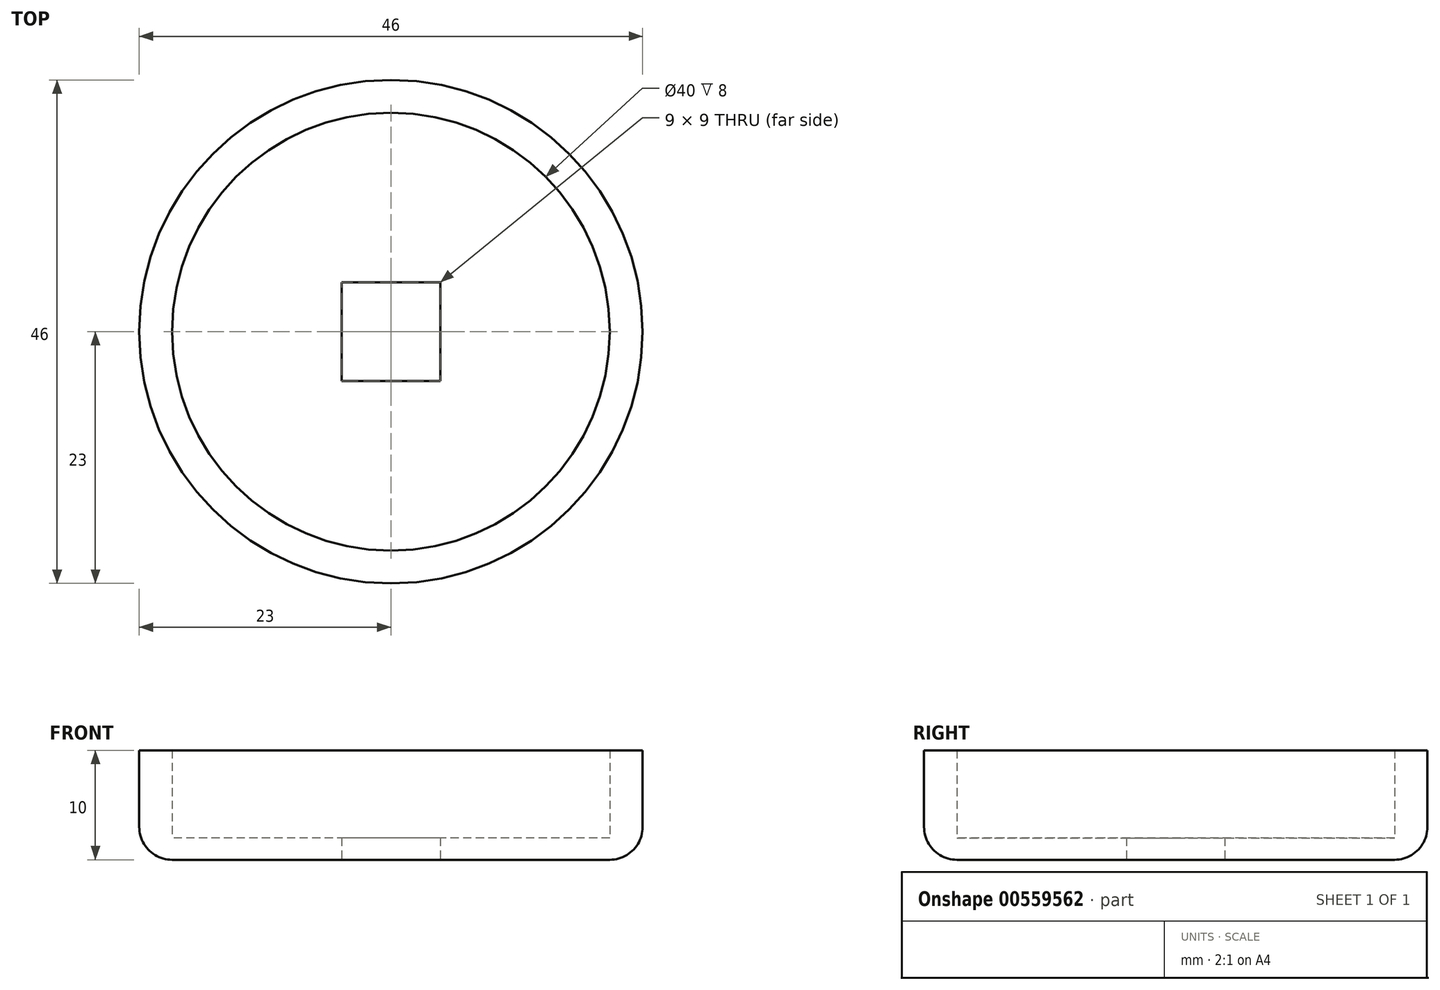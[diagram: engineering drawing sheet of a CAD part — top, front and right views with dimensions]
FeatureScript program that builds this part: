
annotation { "Feature Type Name" : "Feature", "Feature Type Description" : "" }
export const myFeature = defineFeature(function(context is Context, id is Id, definition is map)
    precondition{}
    {
        {
            var Q0;
            Q0=qCreatedBy(makeId("Top.planeOp"),FACE);
            var sketch = newSketch(context, id + "F0", { "sketchPlane" : qUnion([Q0])});
            skCircle(sketch, "E0", {"center": v(0, 0) * mm, "radius": 20 * mm});
            skCircle(sketch, "E1.0", {"center": v(0, 0) * mm, "radius": 23 * mm});
            skLineSegment(sketch, "E2.bottom", {"start": v(4.5, -4.5) * mm, "end": v(-4.5, -4.5) * mm});
            skLineSegment(sketch, "E2.top", {"start": v(4.5, 4.5) * mm, "end": v(-4.5, 4.5) * mm});
            skLineSegment(sketch, "E2.left", {"start": v(4.5, -4.5) * mm, "end": v(4.5, 4.5) * mm});
            skLineSegment(sketch, "E2.right", {"start": v(-4.5, -4.5) * mm, "end": v(-4.5, 4.5) * mm});
            skSolve(sketch);
        }
        {
            var Q0;
            Q0=makeQuery(id+"F0.imprint","IMPRINT",FACE,{"disambiguationData":[TD([[makeQuery(id+"F0.imprint","IMPRINT",EDGE,{"derivedFrom":sQuery(id+"F0.wireOp",EDGE,"E0")}),-1.0]])]});
            extrude(context, id + "F1", {"entities" : qUnion([Q0]), "depth" : 10 * mm, "offsetDistance" : 25 * mm});
        }
        {
            var Q0;
            Q0=qCreatedBy(makeId("Top.planeOp"),FACE);
            var sketch = newSketch(context, id + "F2", { "sketchPlane" : qUnion([Q0])});
            skCircle(sketch, "E3", {"center": v(0, 0) * mm, "radius": 20 * mm});
            skLineSegment(sketch, "E4.bottom", {"start": v(4.5, -4.5) * mm, "end": v(-4.5, -4.5) * mm});
            skLineSegment(sketch, "E4.top", {"start": v(4.5, 4.5) * mm, "end": v(-4.5, 4.5) * mm});
            skLineSegment(sketch, "E4.left", {"start": v(4.5, -4.5) * mm, "end": v(4.5, 4.5) * mm});
            skLineSegment(sketch, "E4.right", {"start": v(-4.5, -4.5) * mm, "end": v(-4.5, 4.5) * mm});
            skSolve(sketch);
        }
        {
            var Q0;
            Q0=makeQuery(id+"F2.imprint","IMPRINT",FACE,{"disambiguationData":[TD([[makeQuery(id+"F2.imprint","IMPRINT",EDGE,{"derivedFrom":sQuery(id+"F2.wireOp",EDGE,"E3")}),1.0]])]});
            extrude(context, id + "F3", {"entities" : qUnion([Q0]), "operationType" : NewBodyOperationType.ADD, "depth" : 2 * mm, "offsetDistance" : 25 * mm});
        }
        {
            var Q0;
            Q0=makeQuery(id+"F1.opExtrude","CAP_EDGE",EDGE,{"disambiguationData":[OSD([sQuery(id+"F0.wireOp",EDGE,"E1.0")])],"isStart":true});
            fillet(context, id + "F4", {"entities" : qUnion([Q0]), "radius" : 3 * mm, "tangentPropagation" : true, "allowEdgeOverflow" : false});
        }
    });
